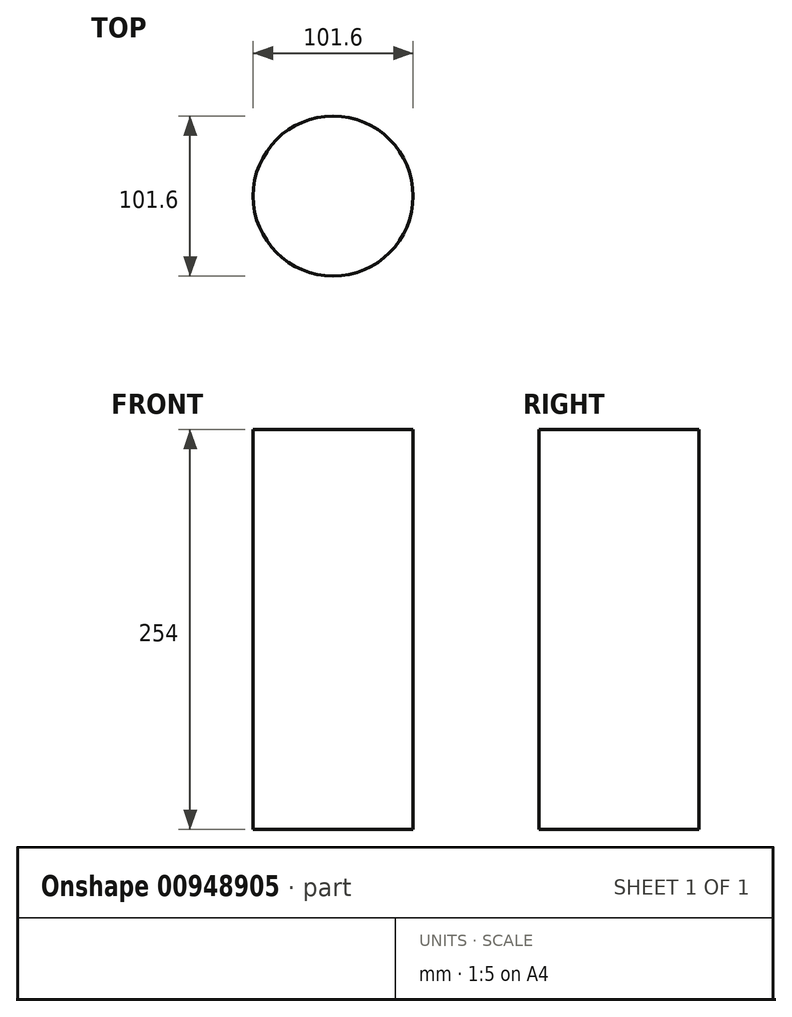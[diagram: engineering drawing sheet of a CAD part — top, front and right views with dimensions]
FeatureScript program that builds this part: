
annotation { "Feature Type Name" : "Feature", "Feature Type Description" : "" }
export const myFeature = defineFeature(function(context is Context, id is Id, definition is map)
    precondition{}
    {
        {
            var Q0;
            Q0=qCreatedBy(makeId("Front.planeOp"),FACE);
            var sketch = newSketch(context, id + "F0", { "sketchPlane" : qUnion([Q0])});
            skLineSegment(sketch, "E0", {"start": v(0, 0) * mm, "end": v(50.8, 0) * mm});
            skLineSegment(sketch, "E1", {"start": v(50.8, 0) * mm, "end": v(50.8, -254) * mm});
            skLineSegment(sketch, "E2", {"start": v(50.8, -254) * mm, "end": v(0, -254) * mm});
            skLineSegment(sketch, "E3", {"start": v(0, -254) * mm, "end": v(0, 0) * mm});
            skSolve(sketch);
        }
        {
            var Q0;
            Q0=qSketchRegion(id+"F0",true);
            var Q1;
            Q1=sQuery(id+"F0.wireOp",EDGE,"E3");
            revolve(context, id + "F1", {"surfaceOperationType" : NewSurfaceOperationType.NEW, "entities" : qUnion([Q0]), "axis" : qUnion([Q1]), "revolveType" : RevolveType.FULL});
        }
    });
